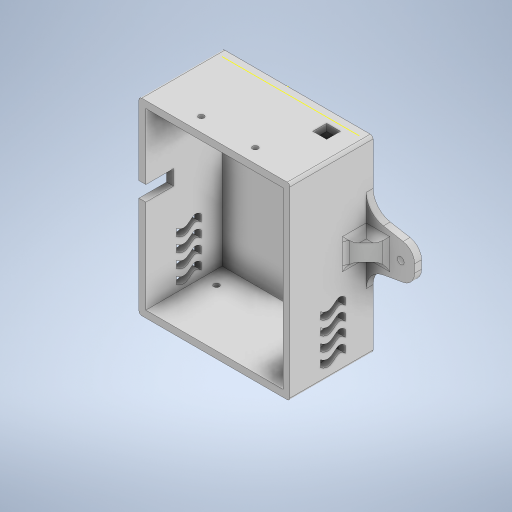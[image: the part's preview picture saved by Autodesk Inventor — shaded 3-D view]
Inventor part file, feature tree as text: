
AUTODESK INVENTOR PART (.ipt)
format: ipt  version: 2024.3 (Build 283343000, 343)  size: 6,096,384 bytes
history: native  units: mm
features: sketch x26, extrude x14, fillet x7, chamfer x6, other x4
ambient origin geometry x8: Origin, YZ Plane, XZ Plane, XY Plane, X Axis, Y Axis, Z Axis, Center Point
bodies: Body1 (feature_tree), Body2 (feature_tree), Body3 (feature_tree), Body4 (feature_tree)
feature tree (57):
  other  "Sólido1"
  extrude  "Extrusión1"  Depth=126.0mm
  extrude  "Extrusión2"  Depth=5.0mm
  fillet  "Empalme1"  Radius=5.0mm
  sketch  "Boceto11"  dims[d8=5.0mm d9=5.0mm]
  extrude  "Extrusión7"  Depth=5.0mm
  extrude  "Extrusión8"  Depth=5.0mm
  chamfer  "Chaflán6"  Distance=55.0mm
  chamfer  "Chaflán7"  Distance=5.0mm
  chamfer  "Chaflán8"  Distance=15.0mm
  chamfer  "Chaflán9"  Distance=14.999mm Angle=135.0deg
  chamfer  "Chaflán10"  Distance=35.0mm
  chamfer  "Chaflán11"  Distance=35.0mm
  extrude  "Extrusión9"  Depth=35.0mm
  fillet  "Empalme3"  Radius=5.0mm
  fillet  "Empalme4"  Radius=10.0mm
  fillet  "Empalme5"  Radius=10.0mm
  fillet  "Empalme6"  Radius=5.0mm
  fillet  "Empalme7"  Radius=58.0mm
  other  "Empalme de cara1"
  other  "Empalme de cara2"
  fillet  "Empalme8"  Radius=10.0mm
  sketch  "Boceto15"  dims[d52=35.0mm]
  extrude  "Extrusión10"  Depth=15.0mm
  sketch  "Boceto17"  dims[d54=55.5mm]
  extrude  "Extrusión11"  Depth=5.0mm
  extrude  "Extrusión12"  Depth=5.0mm
  extrude  "Extrusión13"  Depth=5.0mm
  extrude  "Extrusión14"  Depth=5.0mm
  sketch  "Boceto22"  dims[d64=15.0mm]
  sketch  "Boceto23"  dims[d65=11.5mm]
  sketch  "Boceto24"  dims[d66=11.5mm]
  extrude  "Extrusión15"  Depth=5.0mm
  sketch  "Boceto26"  dims[d68=12.0mm]
  sketch  "Boceto27"  dims[d69=11.5mm d70=15.0mm d71=0.0mm d72=14.999mm d73=2.0mm d74=135.0deg d75=35.0mm d76=2.0mm d77=1.745329mm d78=35.0mm d79=2.0mm d80=1.745329mm]
  extrude  "Extrusión16"  Depth=5.0mm
  sketch  "Boceto29"  dims[d87=15.0mm d88=2.0mm d89=45.0deg d90=5.0mm d91=10.0mm d92=10.0mm d95=5.0mm d96=58.0mm d97=10.0mm]
  sketch  "Boceto30"  dims[d98=5.0mm d99=0.0mm d100=15.0mm]
  extrude  "Extrusión18"  Depth=5.0mm
  sketch  "Boceto33"  dims[d103=5.0mm d104=5.0mm]
  sketch  "Boceto34"  dims[d105=5.0mm d106=5.0mm]
  extrude  "Extrusión19"  Depth=5.0mm
  sketch  "Boceto1"  dims[d0=99.0mm d1=126.0mm]
  sketch  "Boceto2"  dims[d2=109.0mm d3=136.0mm d4=5.0mm d5=5.0mm d6=5.0mm d7=0.0mm]
  sketch  "Boceto12"  dims[d10=5.0mm d11=5.0mm d12=55.0mm d13=0.0mm]
  sketch  "Boceto13"  dims[d14=2.0mm]
  sketch  "Boceto14"  dims[d51=35.0mm]
  sketch  "Boceto16"  dims[d53=45.5mm]
  sketch  "Boceto18"  dims[d55=35.0mm]
  sketch  "Boceto19"  dims[d56=35.0mm]
  sketch  "Boceto20"  dims[d57=45.5mm d58=5.0mm d59=0.0mm]
  sketch  "Boceto21"  dims[d63=12.0mm]
  sketch  "Boceto25"  dims[d67=15.0mm]
  other  "Imagen2"
  sketch  "Boceto28"  dims[d81=35.0mm d82=2.0mm d83=1.745329mm d84=35.0mm d85=2.0mm d86=1.745329mm]
  sketch  "Boceto32"  dims[d101=10.0mm d102=5.0mm]
  sketch  "Boceto35"  dims[d107=5.0mm d108=5.0mm d109=5.0mm d110=5.0mm d111=5.0mm d112=18.0mm d113=18.0mm d114=5.0mm d115=5.0mm d116=5.0mm d117=5.0mm d118=5.0mm d119=5.0mm d120=18.0mm d121=18.0mm d122=5.0mm d123=5.0mm d124=5.0mm d125=5.0mm d126=8.0mm d127=8.0mm d128=15.0mm d129=15.0mm d130=115.0mm d131=0.0mm d132=11.0mm d133=5.5mm d134=20.0mm d135=0.0mm d136=47.5mm d137=67.5mm d138=3.5mm d139=7.0mm d141=4.0mm d142=26.5mm d143=3.5mm d144=4.0mm d145=7.0mm d146=26.5mm d147=10.0mm d148=0.0mm d149=6.5mm d150=6.5mm d151=37.969mm d152=37.969mm d153=3.5mm d154=3.5mm d155=4.0mm d156=4.0mm d157=10.0mm d158=0.0mm d159=10.0mm d160=10.0mm d161=9.5mm d162=41.0mm d163=10.0mm d164=0.0mm d165=58.0mm d166=5.0mm d235=1.0mm d236=0.0mm d241=1.0mm d242=0.0mm d245=2.824866mm d246=2.825mm d247=1.0mm d248=0.0mm d249=10.0mm d250=15.0mm d251=8.0mm d252=5.0mm d253=0.0mm]
